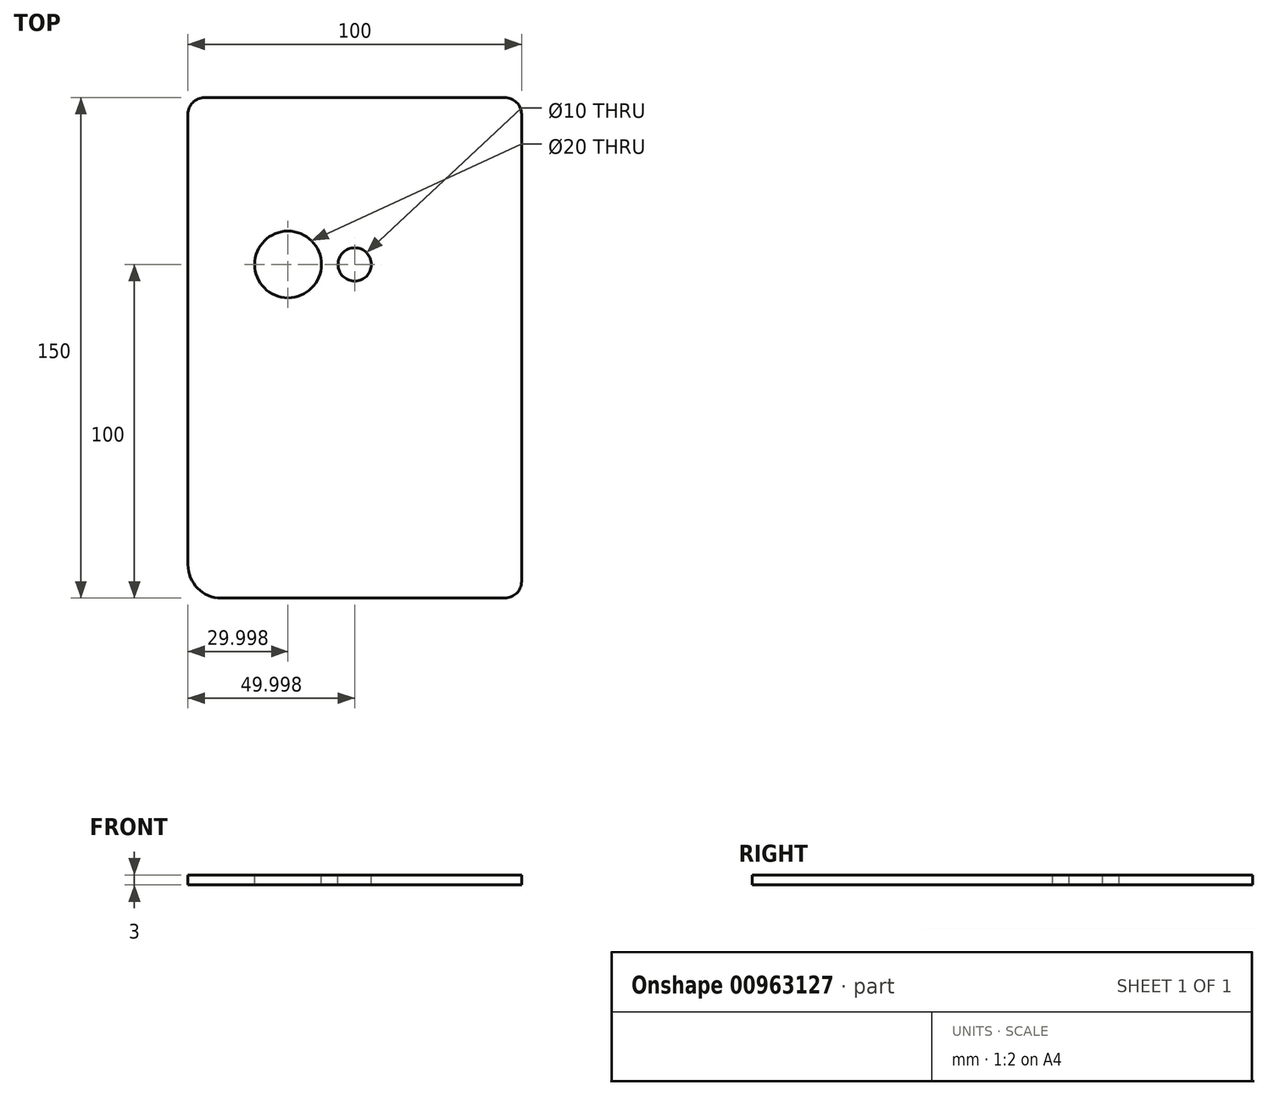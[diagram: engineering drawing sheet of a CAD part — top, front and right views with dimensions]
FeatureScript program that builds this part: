
annotation { "Feature Type Name" : "Feature", "Feature Type Description" : "" }
export const myFeature = defineFeature(function(context is Context, id is Id, definition is map)
    precondition{}
    {
        {
            var Q0;
            Q0=qCreatedBy(makeId("Top.planeOp"),FACE);
            var sketch = newSketch(context, id + "F0", { "sketchPlane" : qUnion([Q0])});
            skLineSegment(sketch, "E0.bottom", {"start": v(-47.73, 113.7) * mm, "end": v(42.27, 113.7) * mm});
            skLineSegment(sketch, "E0.top", {"start": v(-42.73, -36.3) * mm, "end": v(42.27, -36.3) * mm});
            skLineSegment(sketch, "E0.left", {"start": v(-52.73, 108.7) * mm, "end": v(-52.73, -26.3) * mm});
            skLineSegment(sketch, "E0.right", {"start": v(47.27, 108.7) * mm, "end": v(47.27, -31.3) * mm});
            skPoint(sketch, "E1.visualSharp", {"position": v(-52.73, 113.7) * mm});
            skArc(sketch, "E1.filletArc", {"start": v(-47.73, 113.7) * mm, "mid": v(-51.27, 112.24) * mm, "end": v(-52.73, 108.7) * mm});
            skPoint(sketch, "E2.visualSharp", {"position": v(47.27, 113.7) * mm});
            skArc(sketch, "E2.filletArc", {"start": v(47.27, 108.7) * mm, "mid": v(45.8, 112.24) * mm, "end": v(42.27, 113.7) * mm});
            skPoint(sketch, "E3.visualSharp", {"position": v(47.27, -36.3) * mm});
            skArc(sketch, "E3.filletArc", {"start": v(42.27, -36.3) * mm, "mid": v(45.8, -34.84) * mm, "end": v(47.27, -31.3) * mm});
            skPoint(sketch, "E4.visualSharp", {"position": v(-52.73, -36.3) * mm});
            skArc(sketch, "E4.filletArc", {"start": v(-52.73, -26.3) * mm, "mid": v(-49.8, -33.37) * mm, "end": v(-42.73, -36.3) * mm});
            skSolve(sketch);
        }
        {
            var Q0;
            Q0=makeQuery(id+"F0.imprint","IMPRINT",FACE,{"disambiguationData":[TD([[makeQuery(id+"F0.imprint","IMPRINT",EDGE,{"derivedFrom":sQuery(id+"F0.wireOp",EDGE,"E0.bottom")}),-1.0]])]});
            extrude(context, id + "F1", {"entities" : qUnion([Q0]), "depth" : 3 * mm, "offsetDistance" : 25 * mm});
        }
        {
            var Q0;
            Q0=makeQuery(id+"F1.opExtrude","CAP_FACE",FACE,{"disambiguationData":[OSD([sQuery(id+"F0.wireOp",EDGE,"E0.bottom"),sQuery(id+"F0.wireOp",EDGE,"E0.top"),sQuery(id+"F0.wireOp",EDGE,"E0.left"),sQuery(id+"F0.wireOp",EDGE,"E0.right"),sQuery(id+"F0.wireOp",EDGE,"E1.filletArc"),sQuery(id+"F0.wireOp",EDGE,"E2.filletArc"),sQuery(id+"F0.wireOp",EDGE,"E3.filletArc"),sQuery(id+"F0.wireOp",EDGE,"E4.filletArc")])],"isStart":false});
            var sketch = newSketch(context, id + "F2", { "sketchPlane" : qUnion([Q0])});
            skLineSegment(sketch, "E5", {"start": v(-2.73, 113.7) * mm, "end": v(-2.73, 63.7) * mm, "construction": true});
            skLineSegment(sketch, "E6", {"start": v(-2.73, 63.7) * mm, "end": v(-22.73, 63.7) * mm, "construction": true});
            skCircle(sketch, "E7", {"center": v(-22.73, 63.7) * mm, "radius": 10 * mm});
            skCircle(sketch, "E8", {"center": v(-2.73, 63.7) * mm, "radius": 5 * mm});
            skSolve(sketch);
        }
        {
            var Q0;
            Q0=makeQuery(id+"F2.imprint","IMPRINT",FACE,{"disambiguationData":[TD([[makeQuery(id+"F2.imprint","IMPRINT",EDGE,{"derivedFrom":sQuery(id+"F2.wireOp",EDGE,"E7")}),1.0]])]});
            var Q1;
            Q1=makeQuery(id+"F2.imprint","IMPRINT",FACE,{"disambiguationData":[TD([[makeQuery(id+"F2.imprint","IMPRINT",EDGE,{"derivedFrom":sQuery(id+"F2.wireOp",EDGE,"E8")}),1.0]])]});
            extrude(context, id + "F3", {"entities" : qUnion([Q0, Q1]), "operationType" : NewBodyOperationType.REMOVE, "oppositeDirection" : true, "depth" : 25 * mm, "offsetDistance" : 25 * mm});
        }
    });
